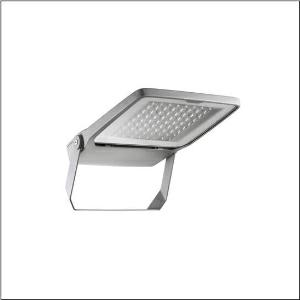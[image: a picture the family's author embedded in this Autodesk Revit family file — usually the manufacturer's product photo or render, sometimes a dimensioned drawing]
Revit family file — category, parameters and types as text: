
# Revit family: floodlight_fl_20_mini___pl61_5xa7672c2c1ac_99ac
name_source: partatom
category: Lighting Fixtures
units: mm (PartAtom-declared; Revit-internal decimal feet)

## family parameters
Cut with Voids When Loaded = No
Host = Face
Light Source = No
Part Type = Normal
Room Calculation Point = No
Round Connector Dimension = Use Diameter
Shared = No

## types (1)
- --- (1 x LED 4000K / CRI = 70 (unbekannt), 12430 lm, 4000K)
    Apparent Load = 96 VA
    CIE Flux Codes = 33 65 98 100 100
    Color Rendering = 70
    Color Temperature = 4000K
    Default Elevation = 1800 mm
    Description = Floodlight FL 20 mini, floodlight, primary light control with lens, of plastic, primary optical cover: protective disc, of toughened safety glass, transparent, light distribution: PL61, light emission: direct distribution, primary light characteristic: asymmetric, installation type: surface-mounted, LED, High Power LED, rated luminous flux: 12.430lm, luminous efficacy: 130lm/W, light colour: 740, colour temperature: 4000K, control gear: ECG Plus, control: flexible luminous flux parameterisation, time-dependent luminous flux control, digital communication interface, power reduction, overheat protection, electronic power reduction, with terminal, 5-pole, max. 2.5mm², mains connection: 220..240V, AC, 50/60Hz, rated input power: 96W, LED unit, of diecast aluminium, powder-coated, Siteco® metallic grey (DB 702S), corrosivity category C5 mid according to DIN EN ISO 12944, incl. 1x M20 cable gland for cable Ø 6.5..12mm, length: 446mm, width: 355mm, height: 62mm, housing frame, of diecast aluminium, powder-coated, Siteco® metallic grey (DB 702S), mounting bracket, of steel, powder-coated, Siteco® metallic grey (DB 702S), DALI, protection rating (complete): IP66, insulation class (complete): insulation class II (safety insulation), certification: CE, ENEC, VDE, protection symbol: D, permissible operating ambient temperature: -40..+40°C, permissible operating ambient temperature for outdoor applications: -40..+50°C, standard: DIN EN 12944, packaging unit: 1 piece

Light Distribution: PL61
    Height = 62 mm  [stored 0.203412 ft]
    Lamp = 1 x LED 4000K / CRI >= 70 (unbekannt)
    Lamp Light Flux = 12430 lm
    Lamp count = 1
    Length = 467 mm
    Luminous efficacy = 130 lm/W
    Manufacturer = Siteco
    ModVariant = No
    Model = 5XA7672C2C1AC
    Mounting Place = Wall
    Mounting Type = Surface mounted
    Number of Poles = 1
    OnlyDefault = Yes
    Power Factor = 1
    Product Name = Floodlight FL 20 mini | PL61
    Product group = floodlight | wall mounted
    ProductGroupID = 2001
    Protection Class = Protection class II
    Protection Degree = IP 66
    RLX_Detail_Level = 1
    RLX_Emergency_Light_Flux = 0 lm
    RLX_Emergency_Type = 0
    RLX_Emergency_Type_DB = No
    RlxData = <blob elided: 74473 chars, md5=97a52f37>
    Socket = socket
    Standby Power = 0 W
    System Light Flux = 12430 lm
    System Power = 96 W
    Type Comments = factory setting: luminous flux: 100 % | dim-lin: 254 | 500 mA
    Type Image = l_1005948.jpg
    URL = http://relux.com
    VarID = @adj_163449
    Voltage = 0 V
    Weight = 0.00 kg
    Width = 335 mm

note: [stored X ft] marks values corroborated as IEEE doubles in the binary element streams (Revit-internal decimal feet)

## geometry (parser evidence)
native form markers: Blend x4, Sweep x13
no freeform markers — native parametric forms only
